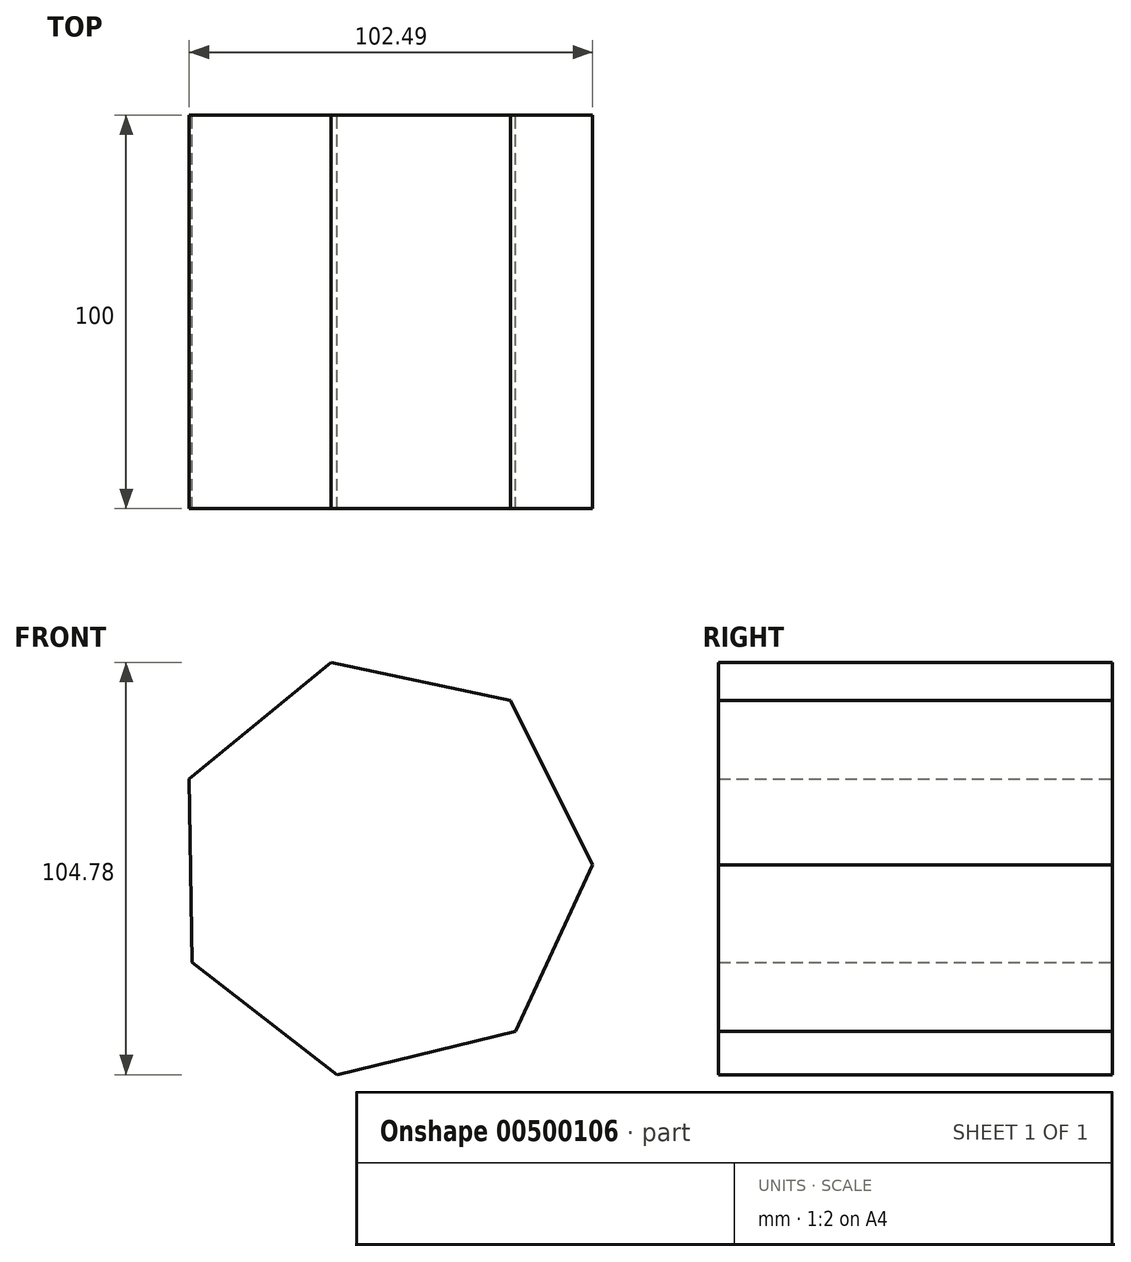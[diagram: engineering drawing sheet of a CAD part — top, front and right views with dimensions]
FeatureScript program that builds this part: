
annotation { "Feature Type Name" : "Feature", "Feature Type Description" : "" }
export const myFeature = defineFeature(function(context is Context, id is Id, definition is map)
    precondition{}
    {
        {
            var Q0;
            Q0=qCreatedBy(makeId("Front.planeOp"),FACE);
            var sketch = newSketch(context, id + "F0", { "sketchPlane" : qUnion([Q0])});
            skCircle(sketch, "E0.cCircle", {"center": v(0, 0) * mm, "radius": 53.74 * mm, "construction": true});
            skLineSegment(sketch, "E0.0", {"start": v(34.1, -41.54) * mm, "end": v(-11.21, -52.56) * mm});
            skLineSegment(sketch, "E0.1", {"start": v(-11.21, -52.56) * mm, "end": v(-48.08, -24) * mm});
            skLineSegment(sketch, "E0.2", {"start": v(-48.08, -24) * mm, "end": v(-48.75, 22.63) * mm});
            skLineSegment(sketch, "E0.3", {"start": v(-48.75, 22.63) * mm, "end": v(-12.7, 52.22) * mm});
            skLineSegment(sketch, "E0.4", {"start": v(-12.7, 52.22) * mm, "end": v(32.9, 42.5) * mm});
            skLineSegment(sketch, "E0.5", {"start": v(32.9, 42.5) * mm, "end": v(53.74, 0.77) * mm});
            skLineSegment(sketch, "E0.6", {"start": v(53.74, 0.77) * mm, "end": v(34.1, -41.54) * mm});
            skSolve(sketch);
        }
        {
            var Q0;
            Q0 = qSketchRegion(id + "F0", true);
            extrude(context, id + "F1", {"entities" : qUnion([Q0]), "endBound" : BoundingType.SYMMETRIC, "depth" : 100 * mm});
        }
    });
